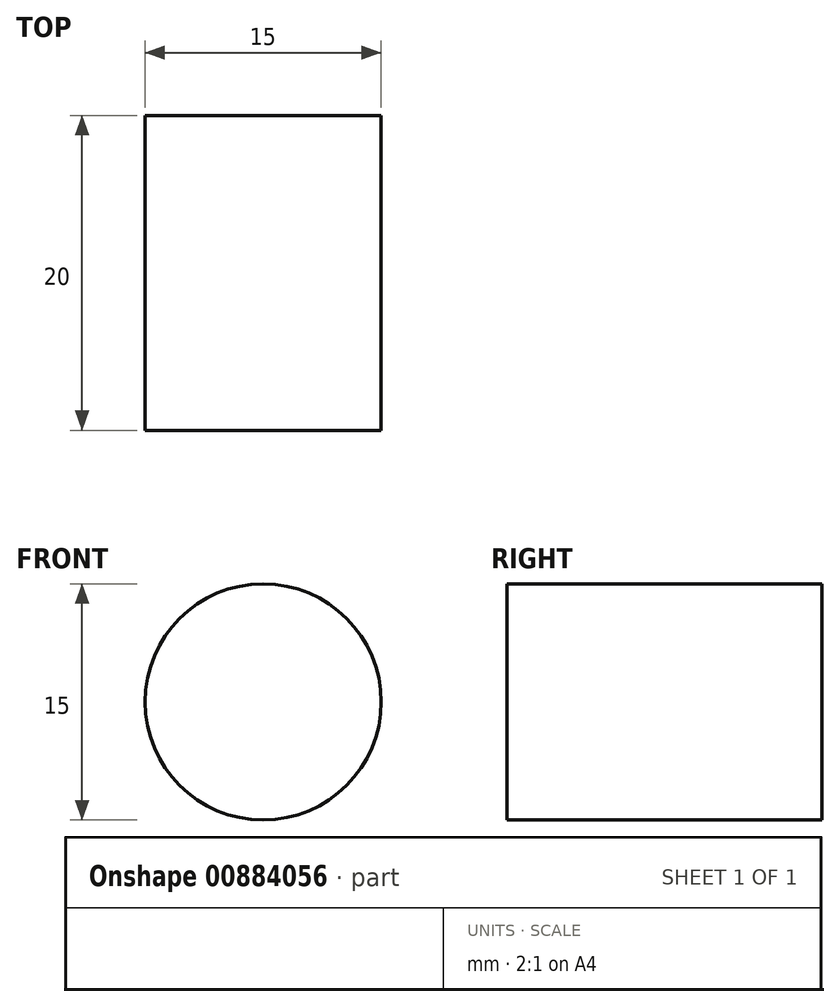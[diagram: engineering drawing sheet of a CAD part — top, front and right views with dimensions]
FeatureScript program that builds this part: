
annotation { "Feature Type Name" : "Feature", "Feature Type Description" : "" }
export const myFeature = defineFeature(function(context is Context, id is Id, definition is map)
    precondition{}
    {
        {
            var Q0;
            Q0=qCreatedBy(makeId("Front.planeOp"),FACE);
            var sketch = newSketch(context, id + "F0", { "sketchPlane" : qUnion([Q0])});
            skCircle(sketch, "E0", {"center": v(0, 0) * mm, "radius": 7.5 * mm});
            skSolve(sketch);
        }
        {
            var Q0;
            Q0=makeQuery(id+"F0.imprint","IMPRINT",FACE,{"disambiguationData":[TD([[makeQuery(id+"F0.imprint","IMPRINT",EDGE,{"derivedFrom":sQuery(id+"F0.wireOp",EDGE,"E0")}),1.0]])]});
            extrude(context, id + "F1", {"entities" : qUnion([Q0]), "depth" : 20 * mm, "offsetDistance" : 25 * mm});
        }
    });
